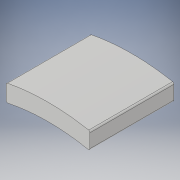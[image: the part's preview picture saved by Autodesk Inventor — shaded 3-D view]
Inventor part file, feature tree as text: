
AUTODESK INVENTOR PART (.ipt)
format: ipt  version: 2019.4 (Build 234330000, 330)  size: 104,960 bytes
history: native  units: mm
features: extrude x1, fillet x1, sketch x1
ambient origin geometry x8: Origin, YZ Plane, XZ Plane, XY Plane, X Axis, Y Axis, Z Axis, Center Point
bodies: Solid1 (feature_tree)
feature tree (3):
  extrude  "Extrusion1"  Depth=0.2mm
  fillet  "Fillet1"  Radius=10.0mm
  sketch  "Sketch1"  dims[d0=51.2mm d1=2.0mm d2=10.0mm d3=5.0mm d4=10.0mm d5=0.0mm d6=0.2mm]
